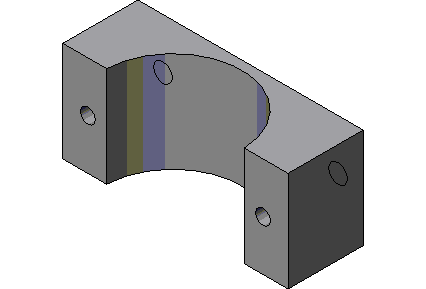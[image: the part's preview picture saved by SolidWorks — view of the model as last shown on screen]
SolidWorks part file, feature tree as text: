
SOLIDWORKS PART (.sldprt)
format: sldprt  version: not decoded by parser v0  size: 186,880 bytes
history: native  units: mm
features: sketch x4, thread x2, extrude x1, cut_extrude x1, hole x1 (+10 scaffold rows collapsed)
feature tree (19):
  scaffold x10  (default folders/planes/origin — collapsed)
  sketch  "Sketch1"  dims[D1=57.15mm D2=19.05mm]
  extrude  "Extrude1"  Depth=25.4mm
  sketch  "Sketch2"  dims[D1=34.925mm D2=0.635mm]
  cut_extrude  "Cut-Extrude1"  [1 undecoded]
  hole  "#10-24 Tapped Hole1"  Diameter=3.7973mm Depth=19.05mm
  sketch  "Sketch4"  dims[D1=44.45mm]
  sketch  "Sketch5"  dims[hole-wizard template sketch: 60 standard entries collapsed; hole parameters kept: c18.Thru Tap Drill Depth=19.05mm]
  thread  "Cosmetic Thread1"  Diameter=4.826mm  [1 undecoded]
  thread  "Cosmetic Thread2"  Diameter=4.826mm  [1 undecoded]
decode coverage: 8 of 9 modeling features carry decoded parameters
note: ~ marks probable driven/reference dimensions
note: 3 parameter values undecoded
note: suppression state not decoded; provenance and decode notes live in map.json
